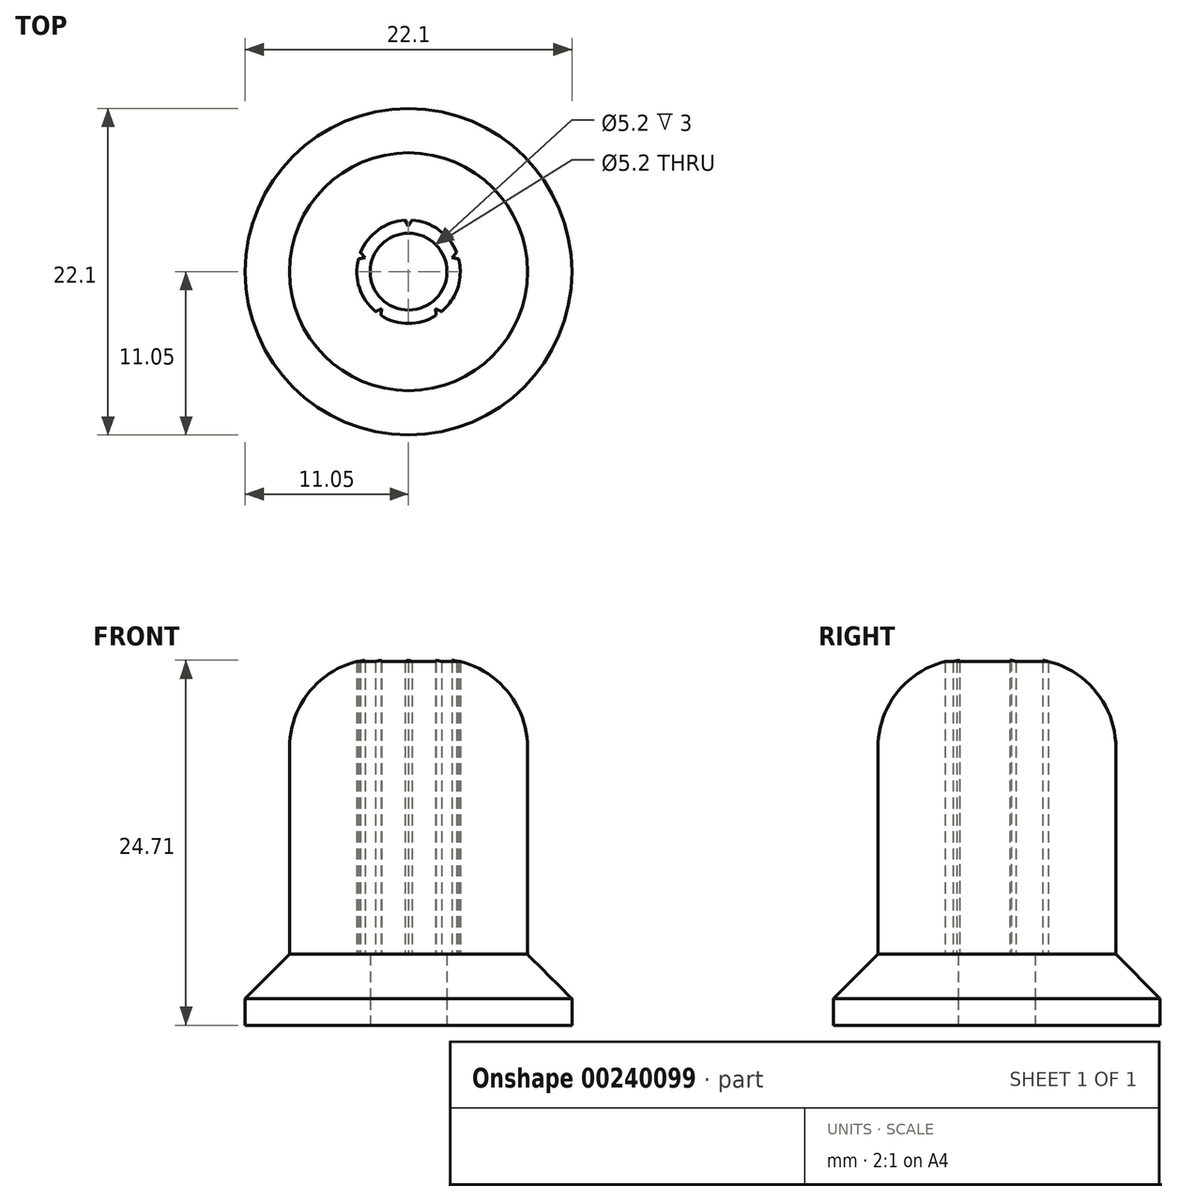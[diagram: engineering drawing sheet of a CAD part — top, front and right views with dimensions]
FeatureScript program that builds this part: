
annotation { "Feature Type Name" : "Feature", "Feature Type Description" : "" }
export const myFeature = defineFeature(function(context is Context, id is Id, definition is map)
    precondition{}
    {
        {
            var Q0;
            Q0=qCreatedBy(makeId("Top.planeOp"),FACE);
            var sketch = newSketch(context, id + "F0", { "sketchPlane" : qUnion([Q0])});
            skCircle(sketch, "E0", {"center": v(0, 0) * mm, "radius": 9.65 * mm, "construction": true});
            skCircle(sketch, "E1.0", {"center": v(0, 0) * mm, "radius": 12.25 * mm, "construction": true});
            skCircle(sketch, "E2.0", {"center": v(0, 0) * mm, "radius": 11.05 * mm});
            skCircle(sketch, "E3", {"center": v(0, 0) * mm, "radius": 2.6 * mm});
            skSolve(sketch);
        }
        {
            var Q0;
            Q0=makeQuery(id+"F0.imprint","IMPRINT",FACE,{"disambiguationData":[TD([[makeQuery(id+"F0.imprint","IMPRINT",EDGE,{"derivedFrom":sQuery(id+"F0.wireOp",EDGE,"E2.0")}),1.0]])]});
            extrude(context, id + "F1", {"entities" : qUnion([Q0]), "depth" : 1.8 * mm});
        }
        {
            var Q0;
            Q0=makeQuery(id+"F1.opExtrude","CAP_FACE",FACE,{"disambiguationData":[OSD([sQuery(id+"F0.wireOp",EDGE,"E2.0"),sQuery(id+"F0.wireOp",EDGE,"E3")])],"isStart":false});
            var sketch = newSketch(context, id + "F2", { "sketchPlane" : qUnion([Q0])});
            skCircle(sketch, "E4.0", {"center": v(0, 0) * mm, "radius": 2.6 * mm});
            skCircle(sketch, "E5.0", {"center": v(0, 0) * mm, "radius": 11.05 * mm});
            skSolve(sketch);
        }
        {
            var Q0;
            Q0=makeQuery(id+"F2.imprint","IMPRINT",FACE,{"disambiguationData":[TD([[makeQuery(id+"F2.imprint","IMPRINT",EDGE,{"derivedFrom":sQuery(id+"F2.wireOp",EDGE,"E4.0")}),-1.0]])]});
            extrude(context, id + "F3", {"entities" : qUnion([Q0]), "depth" : 3 * mm});
        }
        {
            var Q0;
            Q0=makeQuery(id+"F3.opExtrude","CAP_EDGE",EDGE,{"disambiguationData":[OSD([sQuery(id+"F2.wireOp",EDGE,"E5.0")])],"isStart":false});
            chamfer(context, id + "F4", {"entities" : qUnion([Q0]), "width" : 3 * mm, "tangentPropagation" : true});
        }
        {
            var Q0;
            Q0=makeQuery(id+"F3.opExtrude","CAP_FACE",FACE,{"disambiguationData":[OSD([sQuery(id+"F2.wireOp",EDGE,"E4.0"),sQuery(id+"F2.wireOp",EDGE,"E5.0")])],"isStart":false});
            var sketch = newSketch(context, id + "F5", { "sketchPlane" : qUnion([Q0])});
            skPoint(sketch, "E6.0", {"position": v(0, 0) * mm});
            skCircle(sketch, "E7.0", {"center": v(0, 0) * mm, "radius": 8.05 * mm});
            skArc(sketch, "E8", {"start": v(-0.23, 3.5) * mm, "mid": v(-2.06, 2.83) * mm, "end": v(-3.25, 1.3) * mm});
            skLineSegment(sketch, "E9", {"start": v(0, 3.5) * mm, "end": v(0, 3.1) * mm, "construction": true});
            skLineSegment(sketch, "E10", {"start": v(0, 3.1) * mm, "end": v(-0.23, 3.5) * mm});
            skLineSegment(sketch, "E11", {"start": v(0, 3.1) * mm, "end": v(0.23, 3.5) * mm});
            skLineSegment(sketch, "E12.1.0", {"start": v(-2.95, 0.96) * mm, "end": v(-3.4, 0.86) * mm});
            skLineSegment(sketch, "E12.1.1", {"start": v(-2.95, 0.96) * mm, "end": v(-3.25, 1.3) * mm});
            skLineSegment(sketch, "E12.2.0", {"start": v(-1.82, -2.5) * mm, "end": v(-1.87, -2.96) * mm});
            skLineSegment(sketch, "E12.2.1", {"start": v(-1.82, -2.5) * mm, "end": v(-2.24, -2.7) * mm});
            skLineSegment(sketch, "E13.1.3.0", {"start": v(1.82, -2.5) * mm, "end": v(2.24, -2.7) * mm});
            skLineSegment(sketch, "E13.3.3.0", {"start": v(1.82, -2.5) * mm, "end": v(1.87, -2.96) * mm});
            skLineSegment(sketch, "E13.1.4.0", {"start": v(2.95, 0.96) * mm, "end": v(3.25, 1.3) * mm});
            skLineSegment(sketch, "E13.3.4.0", {"start": v(2.95, 0.96) * mm, "end": v(3.4, 0.86) * mm});
            skArc(sketch, "E14.trimOffspring", {"start": v(3.25, 1.3) * mm, "mid": v(2.06, 2.83) * mm, "end": v(0.23, 3.5) * mm});
            skArc(sketch, "E15.trimOffspring", {"start": v(2.24, -2.7) * mm, "mid": v(3.33, -1.08) * mm, "end": v(3.4, 0.86) * mm});
            skArc(sketch, "E16.trimOffspring", {"start": v(-1.87, -2.96) * mm, "mid": v(0, -3.5) * mm, "end": v(1.87, -2.96) * mm});
            skArc(sketch, "E17.trimOffspring", {"start": v(-3.4, 0.86) * mm, "mid": v(-3.33, -1.08) * mm, "end": v(-2.24, -2.7) * mm});
            skSolve(sketch);
        }
        {
            var Q0;
            Q0=makeQuery(id+"F5.imprint","IMPRINT",FACE,{"disambiguationData":[TD([[makeQuery(id+"F5.imprint","IMPRINT",EDGE,{"derivedFrom":sQuery(id+"F5.wireOp",EDGE,"E7.0")}),1.0]])]});
            extrude(context, id + "F6", {"entities" : qUnion([Q0]), "operationType" : NewBodyOperationType.ADD, "depth" : 20 * mm});
        }
        {
            var Q0;
            Q0=makeQuery(id+"F6.opExtrude","CAP_EDGE",EDGE,{"disambiguationData":[OSD([sQuery(id+"F5.wireOp",EDGE,"E7.0")])],"isStart":false});
            fillet(context, id + "F7", {"entities" : qUnion([Q0]), "radius" : 6 * mm, "tangentPropagation" : true, "allowEdgeOverflow" : false});
        }
    });
